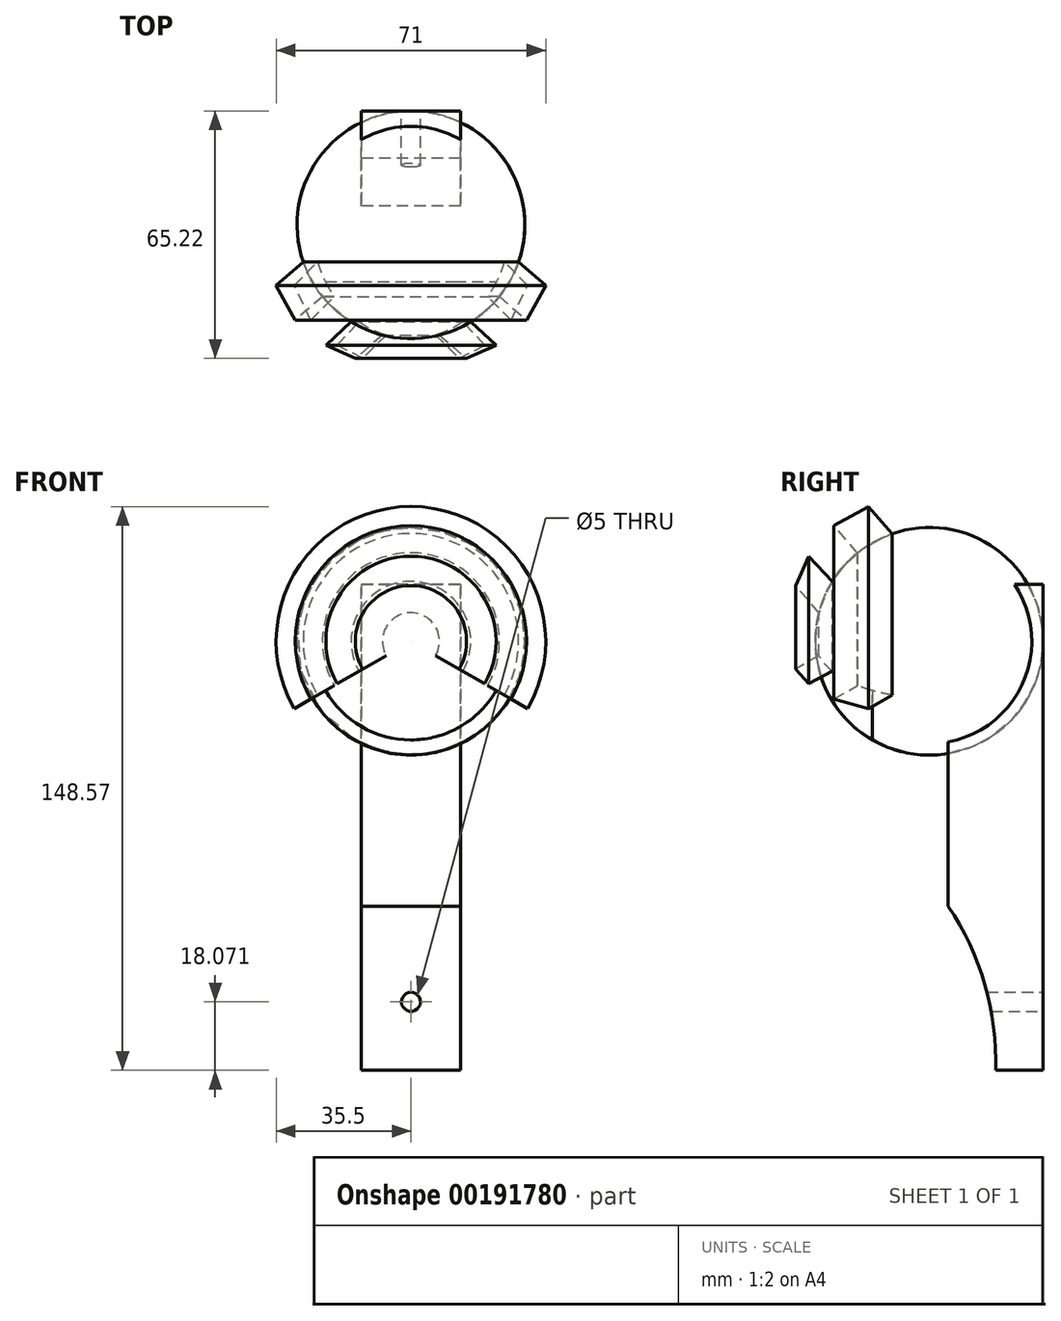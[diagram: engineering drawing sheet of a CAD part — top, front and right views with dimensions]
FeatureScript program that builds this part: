
annotation { "Feature Type Name" : "Feature", "Feature Type Description" : "" }
export const myFeature = defineFeature(function(context is Context, id is Id, definition is map)
    precondition{}
    {
        {
            var Q0;
            Q0=qCreatedBy(makeId("Right.planeOp"),FACE);
            var sketch = newSketch(context, id + "F0", { "sketchPlane" : qUnion([Q0])});
            skArc(sketch, "E0", {"start": v(30, 0) * mm, "mid": v(25.96, 15.04) * mm, "end": v(14.92, 26.03) * mm});
            skLineSegment(sketch, "E1.top", {"start": v(-15.08, -56.66) * mm, "end": v(14.92, -56.66) * mm});
            skArc(sketch, "E2", {"start": v(-15, 25.98) * mm, "mid": v(-20.9, 21.53) * mm, "end": v(-25.52, 15.77) * mm});
            skLineSegment(sketch, "E3", {"start": v(14.92, -56.66) * mm, "end": v(14.92, 26.03) * mm});
            skLineSegment(sketch, "E4", {"start": v(-15.08, -56.66) * mm, "end": v(-15, 25.98) * mm});
            skPoint(sketch, "E5", {"position": v(30, 0) * mm});
            skPoint(sketch, "E6", {"position": v(-30, 0) * mm});
            skPoint(sketch, "E7", {"position": v(0, 30) * mm});
            skArc(sketch, "E8", {"start": v(14.92, 26.03) * mm, "mid": v(-0.05, 30) * mm, "end": v(-15, 25.98) * mm});
            skLineSegment(sketch, "E9", {"start": v(-15.02, 0) * mm, "end": v(63.35, 0) * mm});
            skLineSegment(sketch, "E10", {"start": v(-22.51, 0) * mm, "end": v(-29.04, 7.52) * mm, "construction": true});
            skLineSegment(sketch, "E11", {"start": v(-25.08, 30.42) * mm, "end": v(-18.9, 23.3) * mm});
            skLineSegment(sketch, "E12", {"start": v(-15.94, 35.5) * mm, "end": v(-9.76, 28.37) * mm});
            skLineSegment(sketch, "E13", {"start": v(-4.65, 37.09) * mm, "end": v(1.53, 29.96) * mm});
            skLineSegment(sketch, "E14", {"start": v(7.07, 34.04) * mm, "end": v(13.25, 26.91) * mm});
            skPoint(sketch, "E15", {"position": v(-25.52, 15.77) * mm});
            skPoint(sketch, "E16", {"position": v(-29.04, 7.52) * mm});
            skPoint(sketch, "E17", {"position": v(-18.9, 23.3) * mm});
            skPoint(sketch, "E18", {"position": v(-9.76, 28.37) * mm});
            skPoint(sketch, "E19", {"position": v(1.53, 29.96) * mm});
            skPoint(sketch, "E20", {"position": v(13.25, 26.91) * mm});
            skLineSegment(sketch, "E21", {"start": v(-29.04, 7.52) * mm, "end": v(-35.22, 14.64) * mm});
            skArc(sketch, "E22", {"start": v(-25.52, 15.77) * mm, "mid": v(-28.86, 8.2) * mm, "end": v(-30, 0) * mm});
            skLineSegment(sketch, "E23", {"start": v(-18.9, 23.3) * mm, "end": v(1.3, 0) * mm, "construction": true});
            skLineSegment(sketch, "E24", {"start": v(-9.76, 28.37) * mm, "end": v(14.86, 0) * mm, "construction": true});
            skLineSegment(sketch, "E25", {"start": v(1.53, 29.96) * mm, "end": v(27.52, 0) * mm, "construction": true});
            skLineSegment(sketch, "E26", {"start": v(13.25, 26.91) * mm, "end": v(28.52, 9.32) * mm, "construction": true});
            skLineSegment(sketch, "E27", {"start": v(-25.52, 15.77) * mm, "end": v(-11.83, 0) * mm, "construction": true});
            skLineSegment(sketch, "E28", {"start": v(-35.22, 14.64) * mm, "end": v(-31.7, 22.4) * mm});
            skLineSegment(sketch, "E29", {"start": v(-25.08, 30.42) * mm, "end": v(-15.94, 35.5) * mm});
            skLineSegment(sketch, "E30", {"start": v(-4.65, 37.09) * mm, "end": v(7.07, 34.04) * mm});
            skLineSegment(sketch, "E31", {"start": v(-31.7, 22.4) * mm, "end": v(-25.52, 15.77) * mm});
            skPoint(sketch, "E32", {"position": v(-59.65, 0) * mm});
            skLineSegment(sketch, "E33", {"start": v(-15.02, 0) * mm, "end": v(-59.65, 0) * mm});
            skSolve(sketch);
        }
        {
            var Q0;
            {var subQ0=sQuery(id+"F0.wireOp",EDGE,"E0");Q0=makeQuery(id+"F0.imprint","IMPRINT",FACE,{"disambiguationData":[TD([[makeQuery(id+"F0.imprint","IMPRINT",EDGE,{"derivedFrom":subQ0}),1.0]])]});}
            var Q1;
            {var subQ0=sQuery(id+"F0.wireOp",EDGE,"E8");var subQ1=makeQuery(id+"F0.imprint","INTERSECT",VERTEX,{"derivedFrom":[subQ0,sQuery(id+"F0.wireOp",EDGE,"E13")]});Q1=makeQuery(id+"F0.imprint","IMPRINT",FACE,{"disambiguationData":[TD([[makeQuery(id+"F0.imprint","IMPRINT",EDGE,{"disambiguationData":[TD([[subQ1,1.0]])],"derivedFrom":subQ0}),1.0]])]});}
            var Q2;
            {var subQ0=sQuery(id+"F0.wireOp",EDGE,"E22");var subQ3=makeQuery(id+"F0.imprint","INTERSECT",VERTEX,{"derivedFrom":[sQuery(id+"F0.wireOp",EDGE,"E21"),subQ0]});Q2=makeQuery(id+"F0.imprint","IMPRINT",FACE,{"disambiguationData":[TD([[makeQuery(id+"F0.imprint","IMPRINT",EDGE,{"disambiguationData":[TD([[subQ3,-1.0]])],"derivedFrom":subQ0}),1.0]])]});}
            var Q3;
            Q3=sQuery(id+"F0.wireOp",EDGE,"wQ33m5yY-LGkP-qY01-trcQ-FZKFoT3o34OX");
            var Q4;
            Q4=sQuery(id+"F0.wireOp",EDGE,"E9");
            revolve(context, id + "F1", {"entities" : qUnion([Q0, Q1, Q2]), "surfaceEntities" : qUnion([Q3]), "axis" : qUnion([Q4]), "revolveType" : RevolveType.FULL});
        }
        {
            var Q0;
            {var subQ0=sQuery(id+"F0.wireOp",EDGE,"E21");Q0=makeQuery(id+"F0.imprint","IMPRINT",FACE,{"disambiguationData":[TD([[makeQuery(id+"F0.imprint","IMPRINT",EDGE,{"derivedFrom":subQ0}),-1.0]])]});}
            var Q1;
            {var subQ0=sQuery(id+"F0.wireOp",EDGE,"E11");Q1=makeQuery(id+"F0.imprint","IMPRINT",FACE,{"disambiguationData":[TD([[makeQuery(id+"F0.imprint","IMPRINT",EDGE,{"derivedFrom":subQ0}),1.0]])]});}
            var Q2;
            {var subQ0=sQuery(id+"F0.wireOp",EDGE,"E13");Q2=makeQuery(id+"F0.imprint","IMPRINT",FACE,{"disambiguationData":[TD([[makeQuery(id+"F0.imprint","IMPRINT",EDGE,{"derivedFrom":subQ0}),1.0]])]});}
            var Q3;
            Q3=sQuery(id+"F0.wireOp",EDGE,"E33");
            revolve(context, id + "F2", {"operationType" : NewBodyOperationType.ADD, "entities" : qUnion([Q0, Q1, Q2]), "axis" : qUnion([Q3]), "revolveType" : RevolveType.SYMMETRIC, "angle" : (4 * PI / 3) * radian});
        }
        {
            var Q0;
            Q0=sQuery(id+"F0.wireOp",VERTEX,"E5");
            var Q1;
            Q1=sQuery(id+"F0.wireOp",EDGE,"E9");
            cPlane(context, id + "F3", {"entities" : qUnion([Q0, Q1]), "cplaneType" : CPlaneType.LINE_POINT, "offset" : 25 * mm, "width" : 150 * mm, "height" : 150 * mm});
        }
        {
            var Q0;
            Q0=qCreatedBy(id+"F3.planeOp",FACE);
            var sketch = newSketch(context, id + "F4", { "sketchPlane" : qUnion([Q0])});
            skLineSegment(sketch, "E34.bottom", {"start": v(-13.08, -38.08) * mm, "end": v(13.08, -38.08) * mm});
            skLineSegment(sketch, "E34.left", {"start": v(-13.08, -38.08) * mm, "end": v(-13.08, 15) * mm});
            skLineSegment(sketch, "E34.right", {"start": v(13.08, -38.08) * mm, "end": v(13.08, 15) * mm});
            skPoint(sketch, "E34.middle", {"position": v(0, 0) * mm});
            skPoint(sketch, "E35", {"position": v(-13.08, 15) * mm});
            skLineSegment(sketch, "E36", {"start": v(-13.08, 15) * mm, "end": v(13.08, 15) * mm});
            skPoint(sketch, "E37.orphan", {"position": v(13.08, 15) * mm});
            skSolve(sketch);
        }
        {
            var Q0;
            Q0=makeQuery(id+"F4.imprint","IMPRINT",FACE,{"disambiguationData":[TD([[makeQuery(id+"F4.imprint","IMPRINT",EDGE,{"derivedFrom":sQuery(id+"F4.wireOp",EDGE,"E34.bottom")}),1.0]])]});
            extrude(context, id + "F5", {"entities" : qUnion([Q0]), "operationType" : NewBodyOperationType.ADD, "oppositeDirection" : true, "depth" : 25 * mm});
        }
        {
            var Q0;
            Q0=makeQuery(id+"F5.opExtrude","SWEPT_FACE",FACE,{"disambiguationData":[OSD([sQuery(id+"F4.wireOp",EDGE,"E34.bottom")])]});
            extrude(context, id + "F6", {"entities" : qUnion([Q0]), "operationType" : NewBodyOperationType.ADD, "depth" : 75 * mm});
        }
        {
            var Q0;
            {var subQ0=sQuery(id+"F4.wireOp",EDGE,"E34.right");Q0=makeQuery(id+"F6.boolean.opBoolean","MERGE",FACE,{"derivedFrom":[makeQuery(id+"F5.opExtrude","SWEPT_FACE",FACE,{"disambiguationData":[OSD([subQ0])]}),makeQuery(id+"F6.opExtrude","SWEPT_FACE",FACE,{"disambiguationData":[OSD([sQuery(id+"F4.wireOp",EDGE,"E34.bottom"),subQ0])]})]});}
            var sketch = newSketch(context, id + "F7", { "sketchPlane" : qUnion([Q0])});
            skPoint(sketch, "E38", {"position": v(-17.5, -69.82) * mm});
            skPoint(sketch, "E38.positionSnap0", {"position": v(-17.5, -113.08) * mm});
            skPoint(sketch, "E38.positionSnap1", {"position": v(-5, -69.82) * mm});
            skArc(sketch, "E39", {"start": v(-5, -69.82) * mm, "mid": v(-14.64, -90.47) * mm, "end": v(-17.5, -113.08) * mm});
            skSolve(sketch);
        }
        {
            var Q0;
            {var subQ0=sQuery(id+"F7.wireOp",EDGE,"E39");Q0=makeQuery(id+"F7.imprint","IMPRINT",FACE,{"disambiguationData":[TD([[makeQuery(id+"F7.imprint","IMPRINT",EDGE,{"derivedFrom":subQ0}),1.0]])]});}
            extrude(context, id + "F8", {"entities" : qUnion([Q0]), "operationType" : NewBodyOperationType.REMOVE, "endBound" : BoundingType.THROUGH_ALL, "oppositeDirection" : true, "depth" : 25 * mm});
        }
        {
            var Q0;
            {var subQ0=sQuery(id+"F4.wireOp",EDGE,"E34.bottom");Q0=makeQuery(id+"F6.boolean.opBoolean","MERGE",FACE,{"derivedFrom":[makeQuery(id+"F5.opExtrude","CAP_FACE",FACE,{"disambiguationData":[OSD([subQ0,sQuery(id+"F4.wireOp",EDGE,"E34.left"),sQuery(id+"F4.wireOp",EDGE,"E34.right"),sQuery(id+"F4.wireOp",EDGE,"E36")])],"isStart":true}),makeQuery(id+"F6.opExtrude","SWEPT_FACE",FACE,{"disambiguationData":[OSD([subQ0]),TDD([makeQuery(id+"F5.opExtrude","CAP_EDGE",EDGE,{"disambiguationData":[OSD([subQ0])],"isStart":true})])]})]});}
            var sketch = newSketch(context, id + "F9", { "sketchPlane" : qUnion([Q0])});
            skPoint(sketch, "E40", {"position": v(0, -95) * mm});
            skPoint(sketch, "E40.positionSnap0", {"position": v(0, -113.08) * mm});
            skSolve(sketch);
        }
        {
            var Q0;
            Q0=sQuery(id+"F9.wireOp",VERTEX,"E40");
            var Q1;
            Q1=makeQuery(id+"F1.opRevolve","SWEPT_BODY",BODY,{"disambiguationData":[OSD([sQuery(id+"F0.wireOp",EDGE,"E0"),sQuery(id+"F0.wireOp",EDGE,"E2"),sQuery(id+"F0.wireOp",EDGE,"E8"),sQuery(id+"F0.wireOp",EDGE,"E9"),sQuery(id+"F0.wireOp",EDGE,"E22"),sQuery(id+"F0.wireOp",EDGE,"E33")])]});
            hole(context, id + "F10", {"style" : HoleStyle.SIMPLE, "endStyle" : HoleEndStyle.THROUGH, "holeDiameter" : 5 * mm, "startFromSketch" : true, "locations" : qUnion([Q0]), "scope" : qUnion([Q1]), "isTappedThrough" : true});
        }
    });
